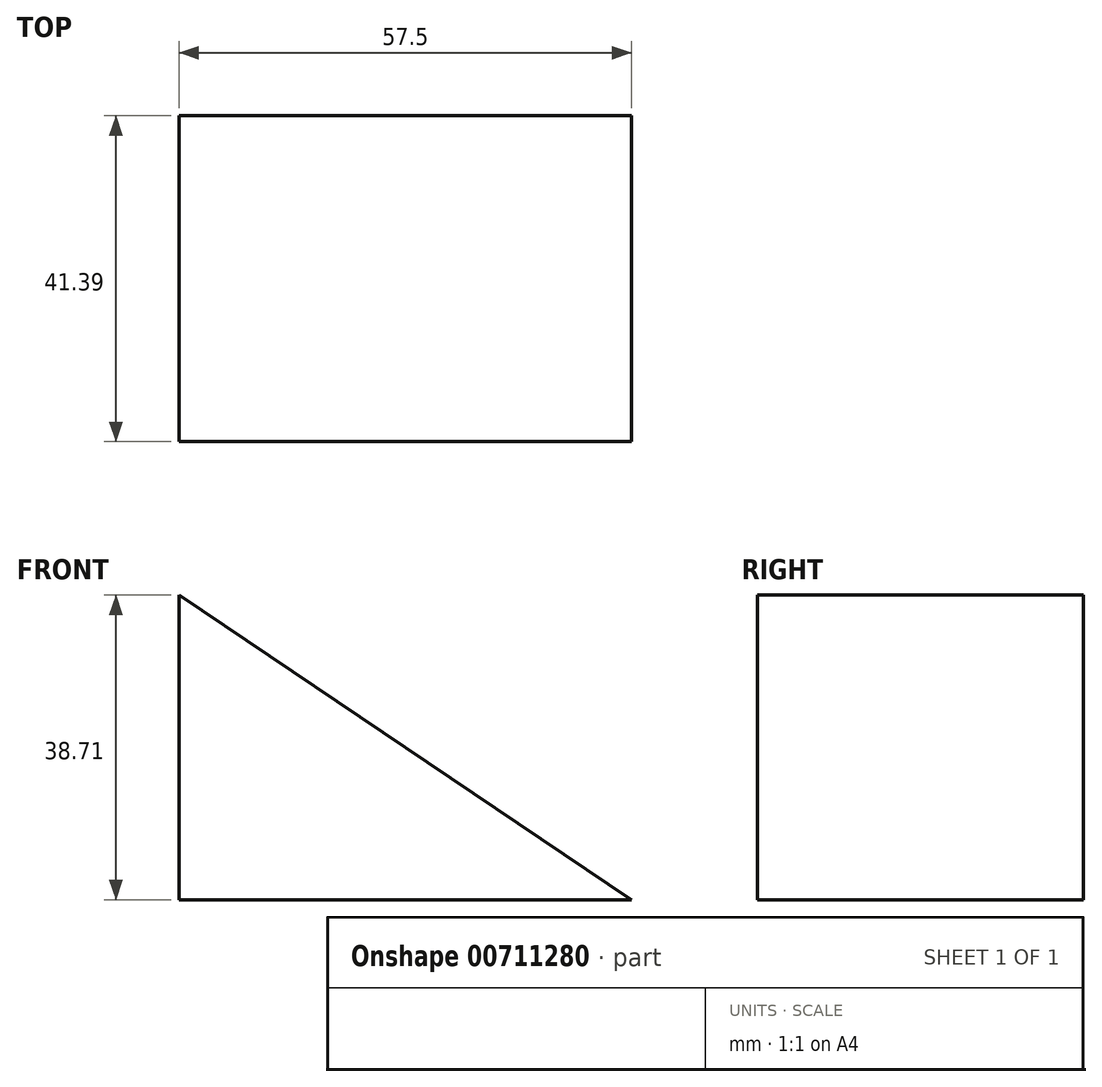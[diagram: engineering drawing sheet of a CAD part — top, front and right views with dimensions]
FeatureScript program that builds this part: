
annotation { "Feature Type Name" : "Feature", "Feature Type Description" : "" }
export const myFeature = defineFeature(function(context is Context, id is Id, definition is map)
    precondition{}
    {
        {
            var Q0;
            Q0=qCreatedBy(makeId("Front.planeOp"),FACE);
            var sketch = newSketch(context, id + "F0", { "sketchPlane" : qUnion([Q0])});
            skLineSegment(sketch, "E0", {"start": v(-57.5, 38.71) * mm, "end": v(0, 0) * mm});
            skLineSegment(sketch, "E1", {"start": v(0, 0) * mm, "end": v(-57.5, 0) * mm});
            skLineSegment(sketch, "E2", {"start": v(-57.5, 0) * mm, "end": v(-57.5, 38.71) * mm});
            skSolve(sketch);
        }
        {
            var Q0;
            Q0=makeQuery(id+"F0.imprint","IMPRINT",FACE,{"disambiguationData":[TD([[makeQuery(id+"F0.imprint","IMPRINT",EDGE,{"derivedFrom":sQuery(id+"F0.wireOp",EDGE,"E0")}),-1.0]])]});
            extrude(context, id + "F1", {"entities" : qUnion([Q0]), "oppositeDirection" : true, "depth" : 41.4 * mm, "offsetDistance" : 25.4 * mm});
        }
        {
            var Q0;
            Q0=makeQuery(id+"F1.opExtrude","CAP_VERTEX",VERTEX,{"disambiguationData":[OSD([sQuery(id+"F0.wireOp",EDGE,"E0"),sQuery(id+"F0.wireOp",EDGE,"E1")])],"isStart":false});
            var Q1;
            Q1=makeQuery(id+"F1.opExtrude","CAP_VERTEX",VERTEX,{"disambiguationData":[OSD([sQuery(id+"F0.wireOp",EDGE,"E0"),sQuery(id+"F0.wireOp",EDGE,"E2")])],"isStart":true});
            var Q2;
            Q2=makeQuery(id+"F1.opExtrude","CAP_VERTEX",VERTEX,{"disambiguationData":[OSD([sQuery(id+"F0.wireOp",EDGE,"E0"),sQuery(id+"F0.wireOp",EDGE,"E2")])],"isStart":false});
            cPlane(context, id + "F2", {"entities" : qUnion([Q0, Q1, Q2]), "cplaneType" : CPlaneType.THREE_POINT, "offset" : 25 * mm, "width" : 150 * mm, "height" : 150 * mm});
        }
    });
